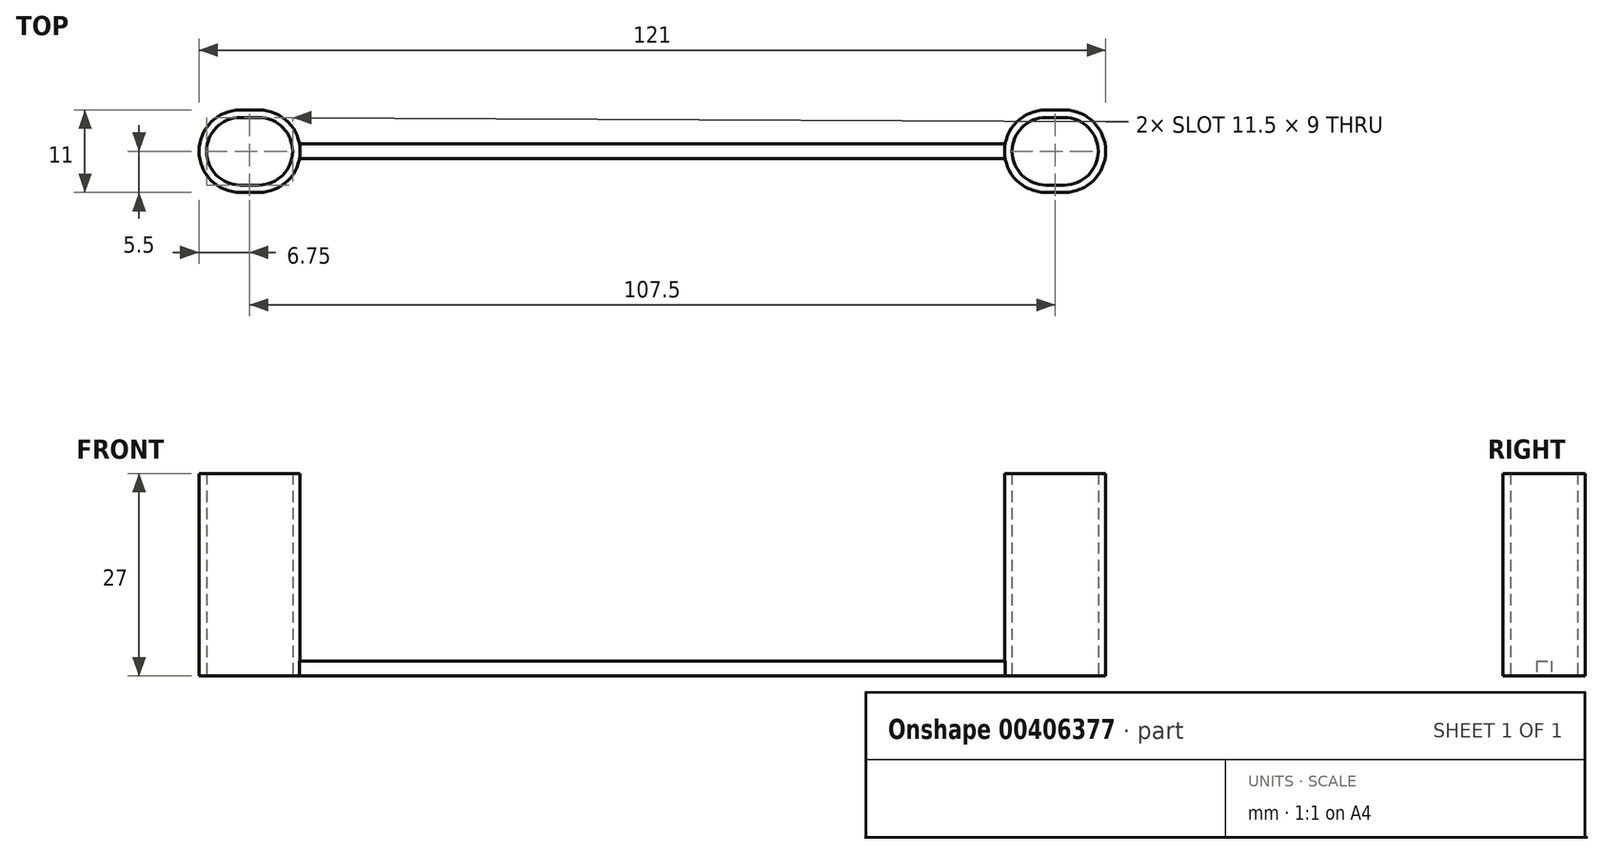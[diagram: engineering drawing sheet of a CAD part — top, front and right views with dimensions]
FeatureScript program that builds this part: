
annotation { "Feature Type Name" : "Feature", "Feature Type Description" : "" }
export const myFeature = defineFeature(function(context is Context, id is Id, definition is map)
    precondition{}
    {
        {
            var Q0;
            Q0=qCreatedBy(makeId("Top.planeOp"),FACE);
            var sketch = newSketch(context, id + "F0", { "sketchPlane" : qUnion([Q0])});
            skArc(sketch, "E0", {"start": v(-52.5, -4.5) * mm, "mid": v(-48, 0) * mm, "end": v(-52.5, 4.5) * mm});
            skArc(sketch, "E1", {"start": v(-55, 4.5) * mm, "mid": v(-59.5, 0) * mm, "end": v(-55, -4.5) * mm});
            skLineSegment(sketch, "E2", {"start": v(-55, 4.5) * mm, "end": v(-52.5, 4.5) * mm});
            skLineSegment(sketch, "E3", {"start": v(-55, -4.5) * mm, "end": v(-52.5, -4.5) * mm});
            skLineSegment(sketch, "E4.0", {"start": v(-55, 5.5) * mm, "end": v(-52.5, 5.5) * mm});
            skArc(sketch, "E4.1", {"start": v(-55, 5.5) * mm, "mid": v(-60.5, 0) * mm, "end": v(-55, -5.5) * mm});
            skLineSegment(sketch, "E4.2", {"start": v(-55, -5.5) * mm, "end": v(-52.5, -5.5) * mm});
            skArc(sketch, "E4.3", {"start": v(-52.5, -5.5) * mm, "mid": v(-47, 0) * mm, "end": v(-52.5, 5.5) * mm});
            skLineSegment(sketch, "E5", {"start": v(0, 1) * mm, "end": v(-47.1, 1) * mm});
            skLineSegment(sketch, "E6", {"start": v(0, -1) * mm, "end": v(-47.1, -1) * mm});
            skLineSegment(sketch, "E7", {"start": v(0, 1) * mm, "end": v(0, -1) * mm});
            skSolve(sketch);
        }
        {
            var Q0;
            Q0=makeQuery(id+"F0.imprint","IMPRINT",FACE,{"disambiguationData":[TD([[makeQuery(id+"F0.imprint","IMPRINT",EDGE,{"derivedFrom":sQuery(id+"F0.wireOp",EDGE,"E0")}),-1.0]])]});
            extrude(context, id + "F1", {"entities" : qUnion([Q0]), "depth" : 27 * mm});
        }
        {
            var Q0;
            {var subQ0=sQuery(id+"F0.wireOp",EDGE,"E5");Q0=makeQuery(id+"F0.imprint","IMPRINT",FACE,{"disambiguationData":[TD([[makeQuery(id+"F0.imprint","IMPRINT",EDGE,{"derivedFrom":subQ0}),1.0]])]});}
            extrude(context, id + "F2", {"entities" : qUnion([Q0]), "operationType" : NewBodyOperationType.ADD, "depth" : 2 * mm});
        }
        {
            var Q0;
            Q0=makeQuery(id+"F1.opExtrude","SWEPT_BODY",BODY,{"disambiguationData":[OSD([sQuery(id+"F0.wireOp",EDGE,"E0"),sQuery(id+"F0.wireOp",EDGE,"E1"),sQuery(id+"F0.wireOp",EDGE,"E2"),sQuery(id+"F0.wireOp",EDGE,"E3"),sQuery(id+"F0.wireOp",EDGE,"E4.0"),sQuery(id+"F0.wireOp",EDGE,"E4.1"),sQuery(id+"F0.wireOp",EDGE,"E4.2"),sQuery(id+"F0.wireOp",EDGE,"E4.3")])]});
            var Q1;
            Q1=qCreatedBy(makeId("Right.planeOp"),FACE);
            mirror(context, id + "F3", {"operationType" : NewBodyOperationType.ADD, "entities" : qUnion([Q0]), "mirrorPlane" : qUnion([Q1])});
        }
    });
